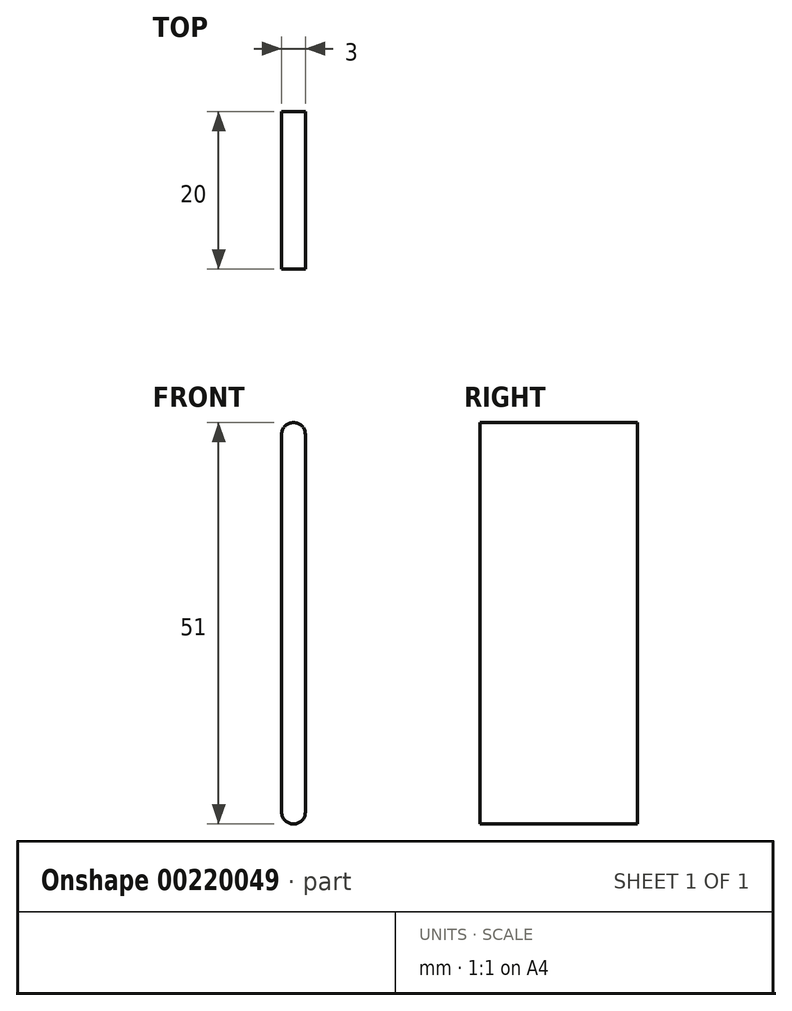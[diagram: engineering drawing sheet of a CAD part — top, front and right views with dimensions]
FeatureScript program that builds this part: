
annotation { "Feature Type Name" : "Feature", "Feature Type Description" : "" }
export const myFeature = defineFeature(function(context is Context, id is Id, definition is map)
    precondition{}
    {
        {
            var Q0;
            Q0=qCreatedBy(makeId("Front.planeOp"),FACE);
            var sketch = newSketch(context, id + "F0", { "sketchPlane" : qUnion([Q0])});
            skLineSegment(sketch, "E0.bottom", {"start": v(-36.1, 36.46) * mm, "end": v(-39.1, 36.46) * mm});
            skLineSegment(sketch, "E0.top", {"start": v(-36.1, -11.54) * mm, "end": v(-39.1, -11.54) * mm});
            skLineSegment(sketch, "E0.left", {"start": v(-36.1, 36.46) * mm, "end": v(-36.1, -11.54) * mm});
            skLineSegment(sketch, "E0.right", {"start": v(-39.1, 36.46) * mm, "end": v(-39.1, -11.54) * mm});
            skArc(sketch, "E1", {"start": v(-39.1, 36.46) * mm, "mid": v(-37.6, 37.96) * mm, "end": v(-36.1, 36.46) * mm});
            skArc(sketch, "E2", {"start": v(-39.1, -11.54) * mm, "mid": v(-37.6, -13.04) * mm, "end": v(-36.1, -11.54) * mm});
            skSolve(sketch);
        }
        {
            var Q0;
            Q0=makeQuery(id+"F0.imprint","IMPRINT",FACE,{"disambiguationData":[TD([[makeQuery(id+"F0.imprint","IMPRINT",EDGE,{"derivedFrom":sQuery(id+"F0.wireOp",EDGE,"E0.bottom")}),1.0]])]});
            var Q1;
            Q1=makeQuery(id+"F0.imprint","IMPRINT",FACE,{"disambiguationData":[TD([[makeQuery(id+"F0.imprint","IMPRINT",EDGE,{"derivedFrom":sQuery(id+"F0.wireOp",EDGE,"E0.bottom")}),-1.0]])]});
            var Q2;
            Q2=makeQuery(id+"F0.imprint","IMPRINT",FACE,{"disambiguationData":[TD([[makeQuery(id+"F0.imprint","IMPRINT",EDGE,{"derivedFrom":sQuery(id+"F0.wireOp",EDGE,"E0.top")}),1.0]])]});
            extrude(context, id + "F1", {"entities" : qUnion([Q0, Q1, Q2]), "depth" : 20 * mm});
        }
    });
